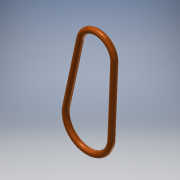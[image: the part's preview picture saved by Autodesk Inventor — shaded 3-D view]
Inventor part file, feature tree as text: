
AUTODESK INVENTOR PART (.ipt)
format: ipt  version: 2019 (Build 230136000, 136)  size: 143,360 bytes
history: native  units: in
note: dims shown in document units (in); Inventor stores cm internally (conversion verified against a paired STEP export)
features: other x4, reference x3, sketch x2, sweep x1
ambient origin geometry x8: Origin, YZ Plane, XZ Plane, XY Plane, X Axis, Y Axis, Z Axis, Center Point
bodies: Solid1 (feature_tree)
feature tree (10):
  sweep  "Sweep1"
  sketch  "Sketch1"  dims[d0=0.5in d1=0.375in]
  reference  "Reference1"
  reference  "Reference2"
  reference  "Reference3"
  sketch  "Sketch2"  dims[d2=0.125in d3=0.0in d4=0.0in]
  parser-record x1  (decoder bookkeeping rows leaked as tree rows — omitted from the tree; the rows remain in map.json)
  other  "Tool_Head_Assem.iam"
  other  "0.75OD_Pulley:1"
  other  "1.0OD_Pulley:1"
note: 1 file-system path scrubbed to <path> (originals preserved in map.json)
